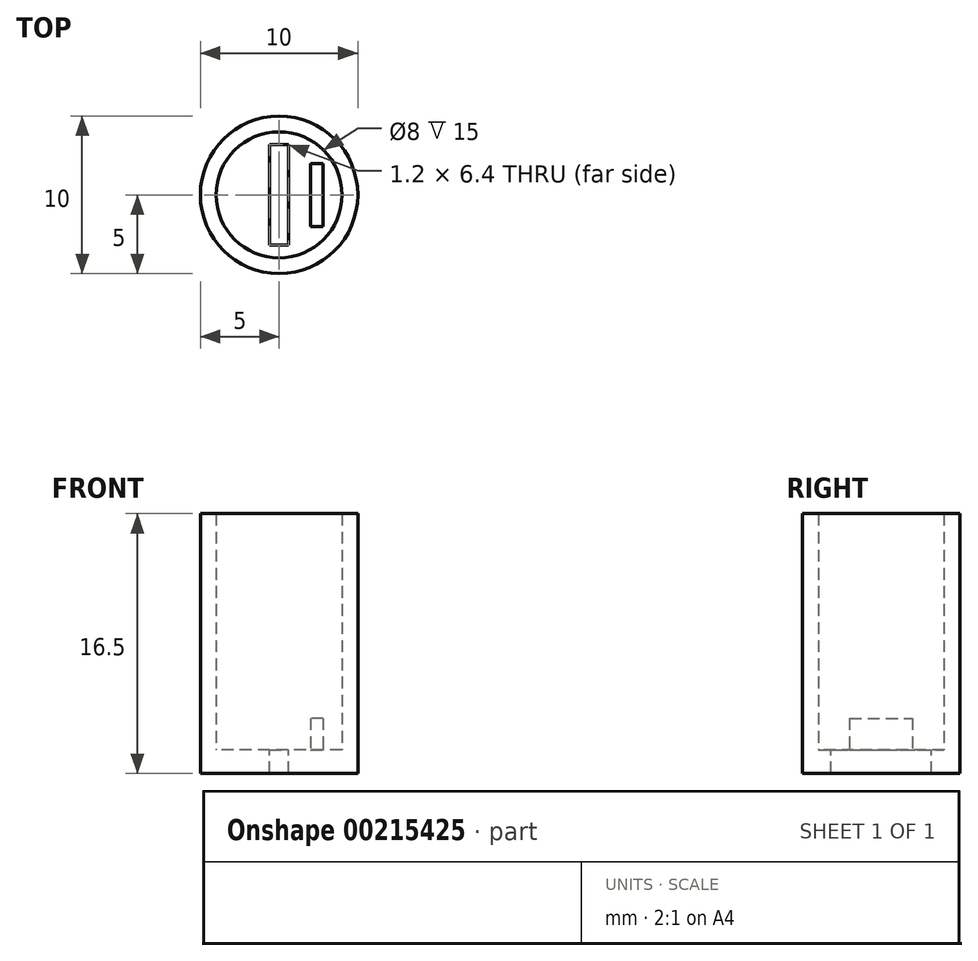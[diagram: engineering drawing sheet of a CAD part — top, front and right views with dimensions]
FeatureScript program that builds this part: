
annotation { "Feature Type Name" : "Feature", "Feature Type Description" : "" }
export const myFeature = defineFeature(function(context is Context, id is Id, definition is map)
    precondition{}
    {
        {
            var Q0;
            Q0=qCreatedBy(makeId("Top.planeOp"),FACE);
            var sketch = newSketch(context, id + "F0", { "sketchPlane" : qUnion([Q0])});
            skCircle(sketch, "E0", {"center": v(0, 0) * mm, "radius": 5 * mm});
            skCircle(sketch, "E1", {"center": v(0, 0) * mm, "radius": 4 * mm});
            skSolve(sketch);
        }
        {
            var Q0;
            Q0 = qSketchRegion(id + "F0", true);
            extrude(context, id + "F1", {"entities" : qUnion([Q0]), "depth" : 15 * mm});
        }
        {
            var Q0;
            Q0=qCreatedBy(makeId("Top.planeOp"),FACE);
            var sketch = newSketch(context, id + "F2", { "sketchPlane" : qUnion([Q0])});
            skCircle(sketch, "E2", {"center": v(0, 0) * mm, "radius": 5 * mm});
            skSolve(sketch);
        }
        {
            var Q0;
            Q0 = qSketchRegion(id + "F2", true);
            extrude(context, id + "F3", {"entities" : qUnion([Q0]), "operationType" : NewBodyOperationType.ADD, "oppositeDirection" : true, "depth" : 1.5 * mm});
        }
        {
            var Q0;
            Q0=qCreatedBy(makeId("Top.planeOp"),FACE);
            var sketch = newSketch(context, id + "F4", { "sketchPlane" : qUnion([Q0])});
            skLineSegment(sketch, "E3", {"start": v(0.6, 3.2) * mm, "end": v(-0.6, 3.2) * mm});
            skLineSegment(sketch, "E4", {"start": v(-0.6, 3.2) * mm, "end": v(-0.6, -3.2) * mm});
            skLineSegment(sketch, "E5", {"start": v(-0.6, -3.2) * mm, "end": v(0.6, -3.2) * mm});
            skLineSegment(sketch, "E6", {"start": v(0.6, -3.2) * mm, "end": v(0.6, 3.2) * mm});
            skSolve(sketch);
        }
        {
            var Q0;
            Q0 = qSketchRegion(id + "F4", true);
            extrude(context, id + "F5", {"entities" : qUnion([Q0]), "operationType" : NewBodyOperationType.REMOVE, "oppositeDirection" : true, "depth" : 2 * mm});
        }
        {
            var Q0;
            Q0=qCreatedBy(makeId("Top.planeOp"),FACE);
            var sketch = newSketch(context, id + "F6", { "sketchPlane" : qUnion([Q0])});
            skLineSegment(sketch, "E7", {"start": v(2, -2) * mm, "end": v(2, 2) * mm});
            skLineSegment(sketch, "E8", {"start": v(2, 2) * mm, "end": v(2.8, 2) * mm});
            skLineSegment(sketch, "E9", {"start": v(2.8, 2) * mm, "end": v(2.8, -2) * mm});
            skLineSegment(sketch, "E10", {"start": v(2.8, -2) * mm, "end": v(2, -2) * mm});
            skSolve(sketch);
        }
        {
            var Q0;
            Q0=makeQuery(id+"F6.imprint","IMPRINT",FACE,{"disambiguationData":[TD([[makeQuery(id+"F6.imprint","IMPRINT",EDGE,{"derivedFrom":sQuery(id+"F6.wireOp",EDGE,"E7")}),-1.0]])]});
            extrude(context, id + "F7", {"entities" : qUnion([Q0]), "operationType" : NewBodyOperationType.ADD, "depth" : 2 * mm});
        }
    });
